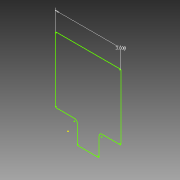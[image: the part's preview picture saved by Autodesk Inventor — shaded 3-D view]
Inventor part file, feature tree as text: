
AUTODESK INVENTOR PART (.ipt)
format: ipt  version: 2013 SP2 (Build 170200200, 200)  size: 105,472 bytes
history: native  units: in
note: dims shown in document units (in); Inventor stores cm internally (conversion verified against a paired STEP export)
features: sketch x1
ambient origin geometry x8: Origin, YZ Plane, XZ Plane, XY Plane, X Axis, Y Axis, Z Axis, Center Point
feature tree (1):
  sketch  "Sketch1"  dims[d0=3.0in]
